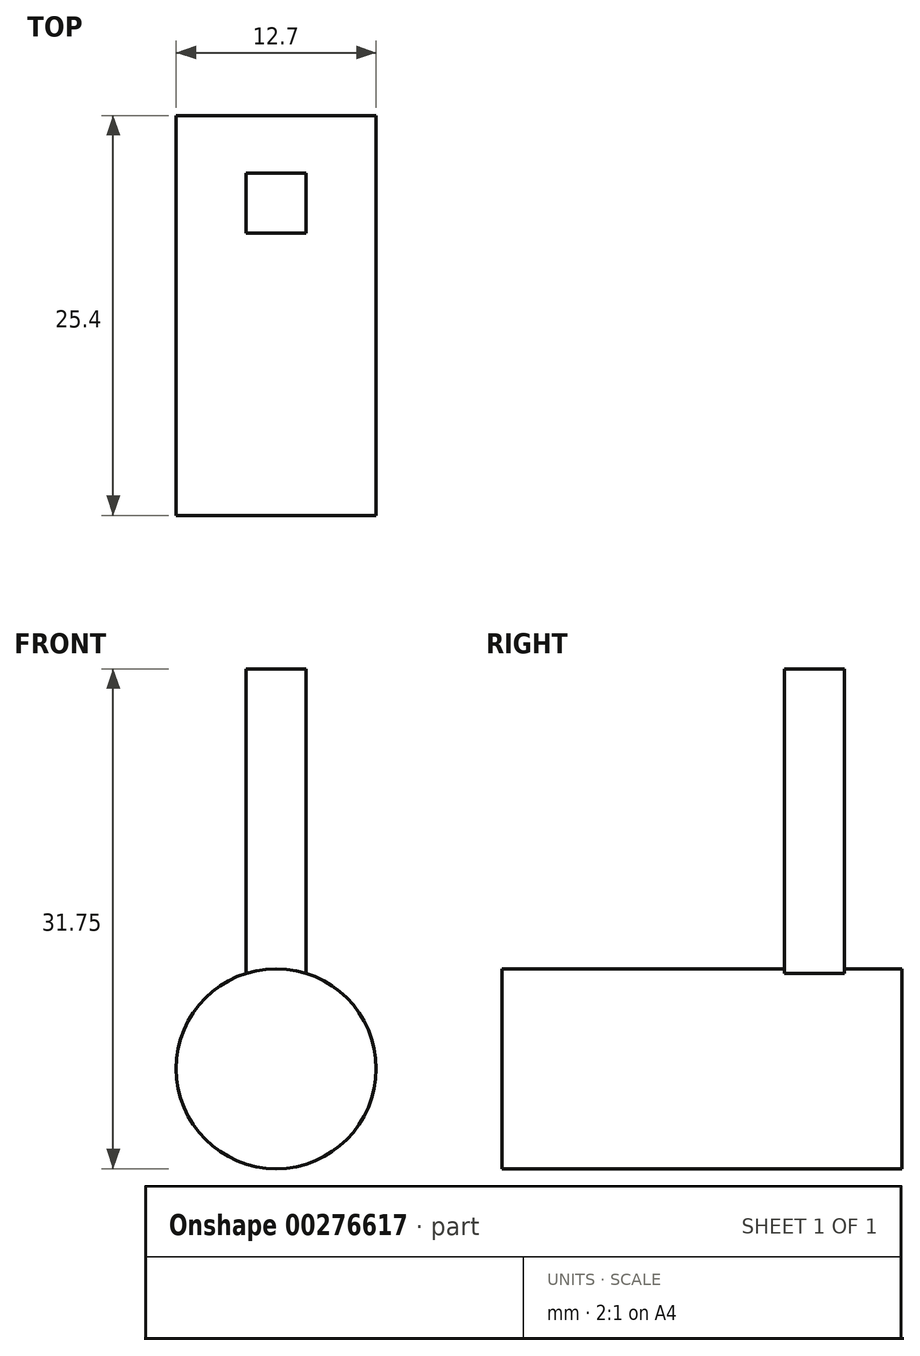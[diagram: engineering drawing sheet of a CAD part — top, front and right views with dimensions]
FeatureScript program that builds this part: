
annotation { "Feature Type Name" : "Feature", "Feature Type Description" : "" }
export const myFeature = defineFeature(function(context is Context, id is Id, definition is map)
    precondition{}
    {
        {
            var Q0;
            Q0=qCreatedBy(makeId("Front.planeOp"),FACE);
            var sketch = newSketch(context, id + "F0", { "sketchPlane" : qUnion([Q0])});
            skCircle(sketch, "E0", {"center": v(0, 0) * mm, "radius": 6.35 * mm});
            skSolve(sketch);
        }
        {
            var Q0;
            Q0 = qSketchRegion(id + "F0", true);
            extrude(context, id + "F1", {"entities" : qUnion([Q0]), "endBound" : BoundingType.SYMMETRIC, "depth" : 25.4 * mm});
        }
        {
            var Q0;
            Q0=qCreatedBy(makeId("Top.planeOp"),FACE);
            var sketch = newSketch(context, id + "F2", { "sketchPlane" : qUnion([Q0])});
            skLineSegment(sketch, "E1.bottom", {"start": v(1.9, 9.05) * mm, "end": v(-1.9, 9.05) * mm});
            skLineSegment(sketch, "E1.top", {"start": v(1.9, 5.24) * mm, "end": v(-1.9, 5.24) * mm});
            skLineSegment(sketch, "E1.left", {"start": v(1.9, 9.05) * mm, "end": v(1.9, 5.24) * mm});
            skLineSegment(sketch, "E1.right", {"start": v(-1.9, 9.05) * mm, "end": v(-1.9, 5.24) * mm});
            skPoint(sketch, "E1.middle", {"position": v(0, 7.14) * mm});
            skSolve(sketch);
        }
        {
            var Q0;
            Q0 = qSketchRegion(id + "F2", true);
            extrude(context, id + "F3", {"entities" : qUnion([Q0]), "operationType" : NewBodyOperationType.ADD, "depth" : 25.4 * mm});
        }
    });
